# Revit family: P200635WX-136c_WDT750SAK_BVWZ
name_source: partatom
category: Specialty Equipment
units: mm (PartAtom-declared; Revit-internal decimal feet)

## family parameters
Always vertical = Yes
Cut with Voids When Loaded = No
Enable Cutting in Views = No
Maintain Annotation Orientation = No
Part Type = Normal
Room Calculation Point = No
Round Connector Dimension = Use Diameter
Shared = No
Work Plane-Based = No

## types (4) — shared parameters
Accent Material = ARCAT - Metal - Steel - Black
Amps = 0 A
Base Fitting Material = ARCAT - Metal - Plastic - Cream
Blanket Material = ARCAT - Fabric - Grey
Body Material = ARCAT - Metal - Plastic - Grey
Clearance Material = ARCAT - Clearance
Default Elevation = 0"
Depth = 26 3/4"
Description = Large Capacity Dishwasher with 3rd Rack
Lave-vaisselle à grande capacité et 3e panier
Dimension Guide = https://www.whirlpool.com
https://www.whirlpool.com
Energy Guide = https://www.whirlpool.com
https://www.whirlpool.com
Family Name = Built In Dishwasher
Feature 1 = 3rd rack
3e panier
Feature 2 = Adjustable 2nd rack
2e panier réglable
Feature 3 = 3-piece silverware basket
Panier à ustensiles à 3 pièces
Height = 33 7/16"
Manufacturer = Whirlpool
Voltage = 0 V
Width = 23 7/8"

## per-type parameters (varying)
| type | Bottom Panel Material | Display Panel Material | Door Material | Handle Material |
| WDT750SAKZ | ARCAT - Metal - Steel - Black | ARCAT - Glass - Black | ARCAT - Metal - Steel - Stainless | ARCAT - Metal - Steel - Stainless |
| WDT750SAKW | ARCAT - Metal - Steel - White | ARCAT - Glass - White | ARCAT - Metal - Steel - White | ARCAT - Metal - Steel - White |
| WDT750SAKB | ARCAT - Metal - Steel - Stainless - Black | ARCAT - Glass - Black | ARCAT - Metal - Steel - Stainless - Black | ARCAT - Metal - Steel - Stainless - Light  Black |
| WDT750SAKV | ARCAT - Metal - Steel - Stainless - Black | ARCAT - Glass - Black | ARCAT - Metal - Steel - Stainless - Black V | ARCAT - Metal - Steel - Stainless - Grey |

note: column(s) folded — value = type name in every type: Model

## geometry (parser evidence)
native form markers: Sweep x5
no freeform markers — native parametric forms only
